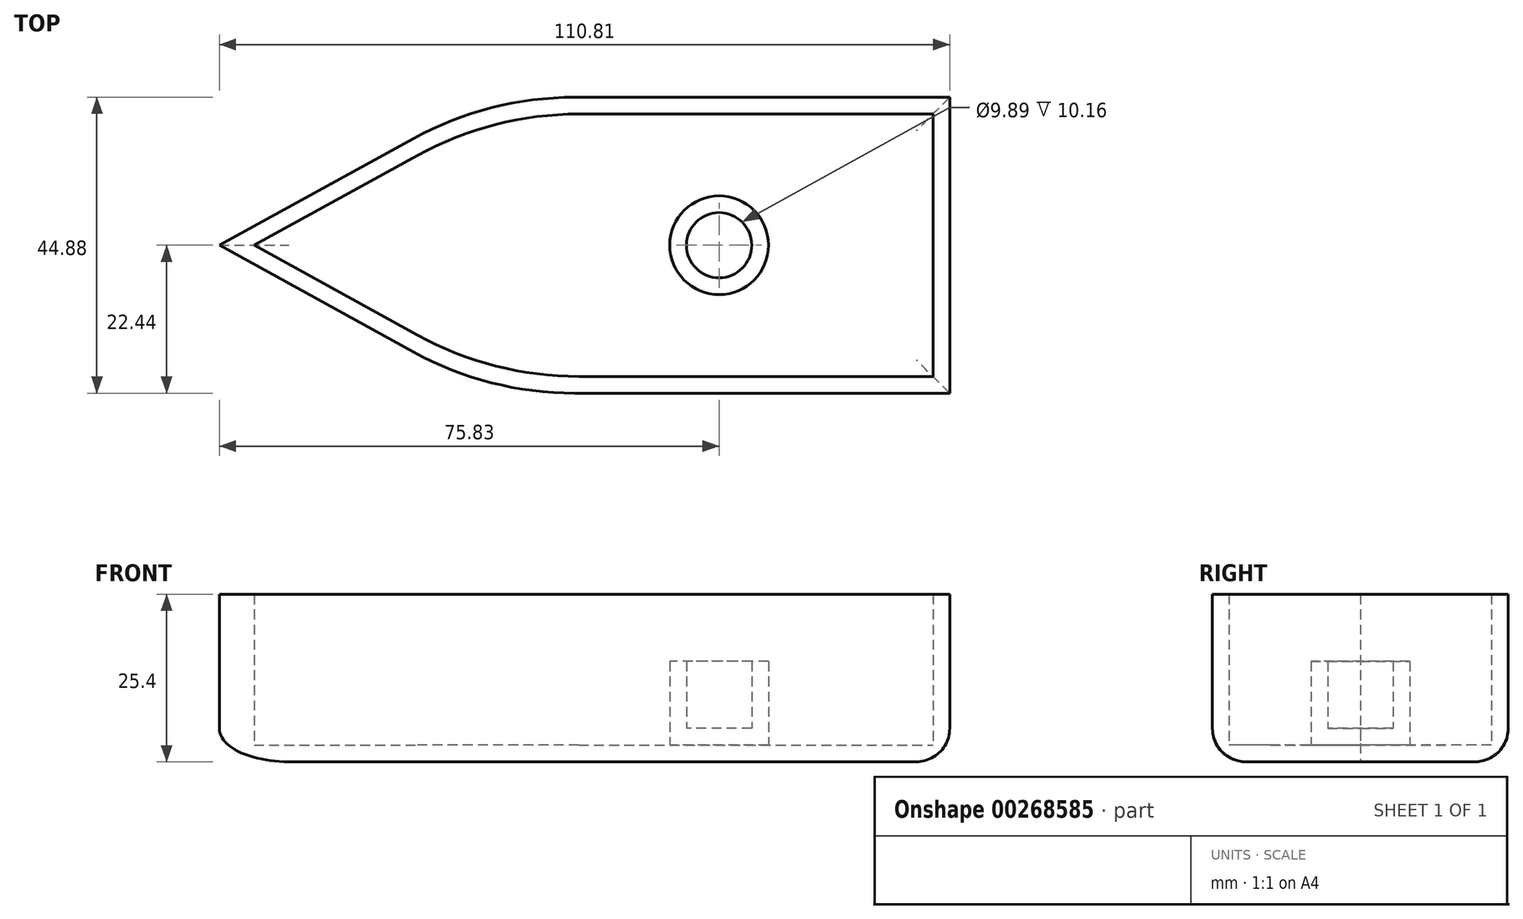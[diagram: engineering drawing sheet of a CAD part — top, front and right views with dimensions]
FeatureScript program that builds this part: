
annotation { "Feature Type Name" : "Feature", "Feature Type Description" : "" }
export const myFeature = defineFeature(function(context is Context, id is Id, definition is map)
    precondition{}
    {
        {
            var Q0;
            Q0=qCreatedBy(makeId("Top.planeOp"),FACE);
            var sketch = newSketch(context, id + "F0", { "sketchPlane" : qUnion([Q0])});
            skLineSegment(sketch, "E0.bottom", {"start": v(-34.98, 22.44) * mm, "end": v(34.98, 22.44) * mm});
            skLineSegment(sketch, "E0.top", {"start": v(-34.98, -22.44) * mm, "end": v(34.98, -22.44) * mm});
            skLineSegment(sketch, "E0.right", {"start": v(34.98, 22.44) * mm, "end": v(34.98, -22.44) * mm});
            skPoint(sketch, "E0.middle", {"position": v(0, 0) * mm});
            skLineSegment(sketch, "E1", {"start": v(-34.98, -22.44) * mm, "end": v(-75.83, 0) * mm});
            skLineSegment(sketch, "E2", {"start": v(-75.83, 0) * mm, "end": v(-34.98, 22.44) * mm});
            skSolve(sketch);
        }
        {
            var Q0;
            Q0=makeQuery(id+"F0.imprint","IMPRINT",FACE,{"disambiguationData":[TD([[makeQuery(id+"F0.imprint","IMPRINT",EDGE,{"derivedFrom":sQuery(id+"F0.wireOp",EDGE,"E0.bottom")}),-1.0]])]});
            extrude(context, id + "F1", {"entities" : qUnion([Q0]), "depth" : 25.4 * mm});
        }
        {
            var Q0;
            Q0=makeQuery(id+"F1.opExtrude","CAP_FACE",FACE,{"disambiguationData":[OSD([sQuery(id+"F0.wireOp",EDGE,"E0.bottom"),sQuery(id+"F0.wireOp",EDGE,"E0.top"),sQuery(id+"F0.wireOp",EDGE,"E0.right"),sQuery(id+"F0.wireOp",EDGE,"E1"),sQuery(id+"F0.wireOp",EDGE,"E2")])],"isStart":false});
            shell(context, id + "F2", {"entities" : qUnion([Q0]), "thickness" : 2.54 * mm});
        }
        {
            var Q0;
            Q0=makeQuery(id+"F1.opExtrude","CAP_EDGE",EDGE,{"disambiguationData":[OSD([sQuery(id+"F0.wireOp",EDGE,"E0.top")])],"isStart":true});
            var Q1;
            Q1=makeQuery(id+"F1.opExtrude","CAP_EDGE",EDGE,{"disambiguationData":[OSD([sQuery(id+"F0.wireOp",EDGE,"E1")])],"isStart":true});
            var Q2;
            Q2=makeQuery(id+"F1.opExtrude","CAP_EDGE",EDGE,{"disambiguationData":[OSD([sQuery(id+"F0.wireOp",EDGE,"E2")])],"isStart":true});
            var Q3;
            Q3=makeQuery(id+"F1.opExtrude","CAP_EDGE",EDGE,{"disambiguationData":[OSD([sQuery(id+"F0.wireOp",EDGE,"E0.bottom")])],"isStart":true});
            var Q4;
            Q4=makeQuery(id+"F1.opExtrude","CAP_EDGE",EDGE,{"disambiguationData":[OSD([sQuery(id+"F0.wireOp",EDGE,"E0.right")])],"isStart":true});
            fillet(context, id + "F3", {"entities" : qUnion([Q0, Q1, Q2, Q3, Q4]), "radius" : 5.08 * mm, "tangentPropagation" : true, "allowEdgeOverflow" : false});
        }
        {
            var Q0;
            Q0=makeQuery(id+"F1.opExtrude","SWEPT_EDGE",EDGE,{"disambiguationData":[OSD([sQuery(id+"F0.wireOp",EDGE,"E0.top"),sQuery(id+"F0.wireOp",EDGE,"E1")])]});
            var Q1;
            Q1=makeQuery(id+"F1.opExtrude","SWEPT_EDGE",EDGE,{"disambiguationData":[OSD([sQuery(id+"F0.wireOp",EDGE,"E0.bottom"),sQuery(id+"F0.wireOp",EDGE,"E2")])]});
            var Q2;
            Q2=makeQuery(id+"F2.opShell","OFFSET_EDGE",EDGE,{"disambiguationData":[OSD([sQuery(id+"F0.wireOp",EDGE,"E0.top"),sQuery(id+"F0.wireOp",EDGE,"E1")])]});
            var Q3;
            Q3=makeQuery(id+"F2.opShell","OFFSET_EDGE",EDGE,{"disambiguationData":[OSD([sQuery(id+"F0.wireOp",EDGE,"E0.bottom"),sQuery(id+"F0.wireOp",EDGE,"E2")])]});
            fillet(context, id + "F4", {"entities" : qUnion([Q0, Q1, Q2, Q3]), "radius" : 50.8 * mm, "tangentPropagation" : true, "allowEdgeOverflow" : false});
        }
        {
            var Q0;
            Q0=makeQuery(id+"F2.opShell","OFFSET_FACE",FACE,{"disambiguationData":[OSD([sQuery(id+"F0.wireOp",EDGE,"E0.bottom"),sQuery(id+"F0.wireOp",EDGE,"E0.top"),sQuery(id+"F0.wireOp",EDGE,"E0.right"),sQuery(id+"F0.wireOp",EDGE,"E1"),sQuery(id+"F0.wireOp",EDGE,"E2")])]});
            var sketch = newSketch(context, id + "F5", { "sketchPlane" : qUnion([Q0])});
            skCircle(sketch, "E3", {"center": v(0, 0) * mm, "radius": 7.49 * mm});
            skSolve(sketch);
        }
        {
            var Q0;
            Q0=makeQuery(id+"F5.imprint","IMPRINT",FACE,{"disambiguationData":[TD([[makeQuery(id+"F5.imprint","IMPRINT",EDGE,{"derivedFrom":sQuery(id+"F5.wireOp",EDGE,"E3")}),1.0]])]});
            var Q1;
            Q1=sQuery(id+"F5.wireOp",EDGE,"lODUlXpu-Lyvv-ZOdb-rXvb-ZiEmtah8B92Q");
            extrude(context, id + "F6", {"entities" : qUnion([Q0]), "surfaceEntities" : qUnion([Q1]), "depth" : 12.7 * mm});
        }
        {
            var Q0;
            Q0=makeQuery(id+"F6.opExtrude","CAP_FACE",FACE,{"disambiguationData":[OSD([sQuery(id+"F5.wireOp",EDGE,"E3")])],"isStart":false});
            shell(context, id + "F7", {"entities" : qUnion([Q0]), "thickness" : 2.54 * mm});
        }
    });
